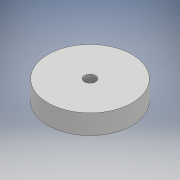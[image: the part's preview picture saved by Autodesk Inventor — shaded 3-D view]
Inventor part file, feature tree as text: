
AUTODESK INVENTOR PART (.ipt)
format: ipt  version: 2017 (Build 210142000, 142)  size: 94,720 bytes
history: native  units: mm
features: revolve x1, sketch x1
ambient origin geometry x8: Origin, YZ Plane, XZ Plane, XY Plane, X Axis, Y Axis, Z Axis, Center Point
bodies: Solid1 (feature_tree)
feature tree (2):
  revolve  "Revolution1"  Angle=90.0deg
  sketch  "Sketch1"  dims[d0=2.5mm d1=90.0deg]
